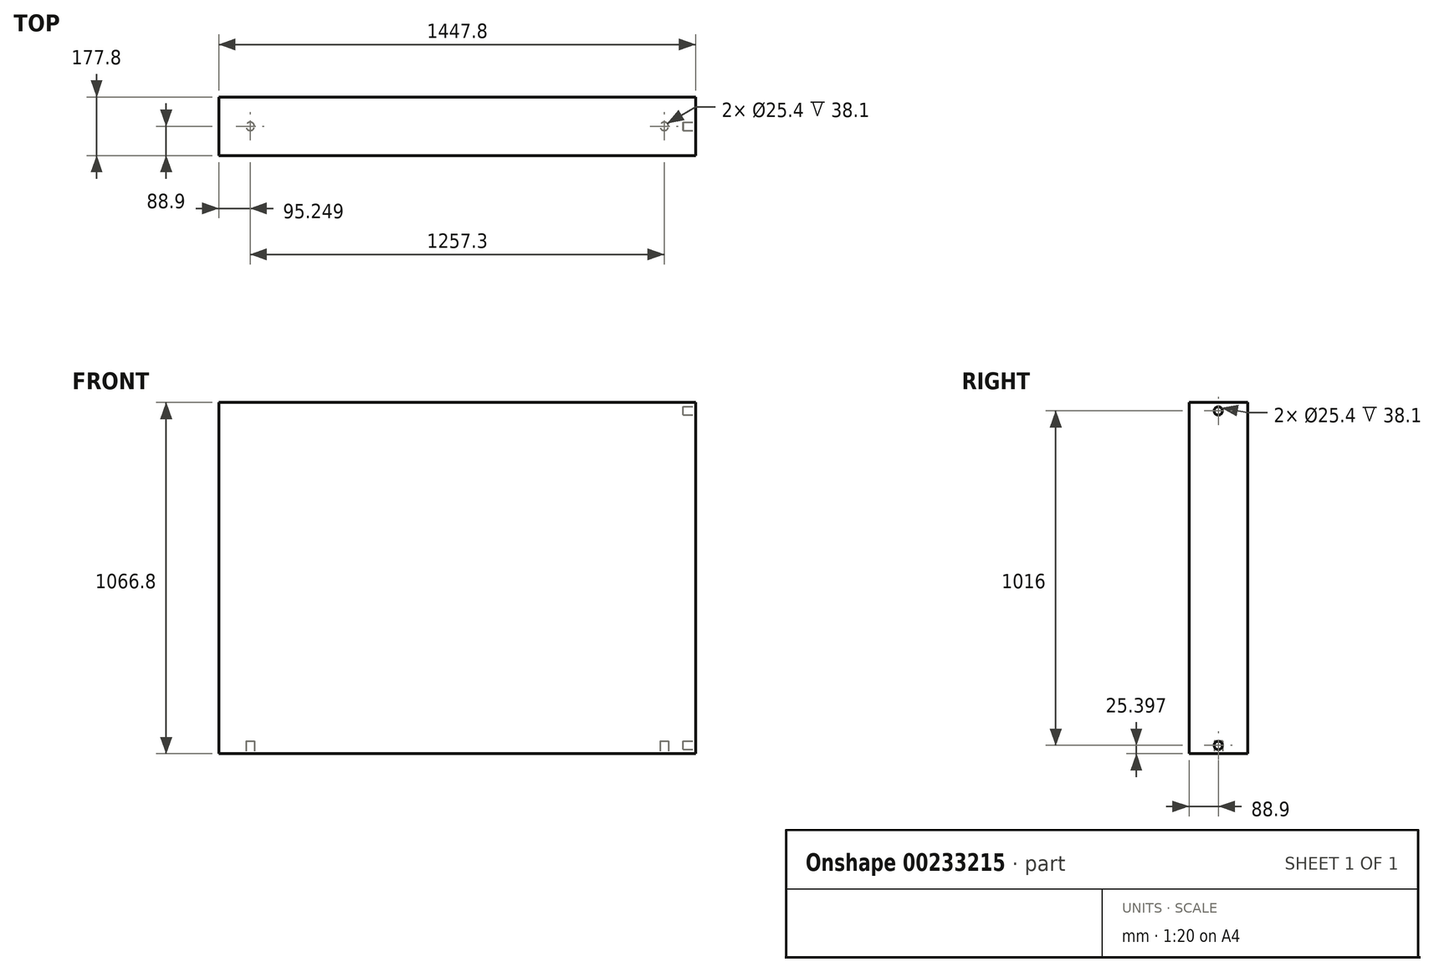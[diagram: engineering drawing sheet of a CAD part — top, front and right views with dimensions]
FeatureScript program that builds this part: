
annotation { "Feature Type Name" : "Feature", "Feature Type Description" : "" }
export const myFeature = defineFeature(function(context is Context, id is Id, definition is map)
    precondition{}
    {
        {
            var Q0;
            Q0=qCreatedBy(makeId("Front.planeOp"),FACE);
            var sketch = newSketch(context, id + "F0", { "sketchPlane" : qUnion([Q0])});
            skLineSegment(sketch, "E0.bottom", {"start": v(-749.86, 115.38) * mm, "end": v(697.94, 115.38) * mm});
            skLineSegment(sketch, "E0.top", {"start": v(-749.86, -951.42) * mm, "end": v(697.94, -951.42) * mm});
            skLineSegment(sketch, "E0.left", {"start": v(-749.86, 115.38) * mm, "end": v(-749.86, -951.42) * mm});
            skLineSegment(sketch, "E0.right", {"start": v(697.94, 115.38) * mm, "end": v(697.94, -951.42) * mm});
            skSolve(sketch);
        }
        {
            var Q0;
            Q0 = qSketchRegion(id + "F0", true);
            extrude(context, id + "F1", {"entities" : qUnion([Q0]), "depth" : 177.8 * mm});
        }
        {
            var Q0;
            Q0=makeQuery(id+"F1.opExtrude","SWEPT_FACE",FACE,{"disambiguationData":[OSD([sQuery(id+"F0.wireOp",EDGE,"E0.top")])]});
            var sketch = newSketch(context, id + "F2", { "sketchPlane" : qUnion([Q0])});
            skCircle(sketch, "E1", {"center": v(-654.61, 88.9) * mm, "radius": 12.7 * mm});
            skLineSegment(sketch, "E2", {"start": v(-657.5, 177.8) * mm, "end": v(-749.86, 177.8) * mm});
            skLineSegment(sketch, "E3", {"start": v(-749.86, 177.8) * mm, "end": v(-749.86, 0) * mm});
            skLineSegment(sketch, "E4", {"start": v(-749.86, 0) * mm, "end": v(-659.45, 0) * mm});
            skCircle(sketch, "E5", {"center": v(602.69, 88.9) * mm, "radius": 12.7 * mm});
            skLineSegment(sketch, "E6", {"start": v(591.78, 177.8) * mm, "end": v(697.94, 177.8) * mm});
            skLineSegment(sketch, "E7", {"start": v(697.94, 177.8) * mm, "end": v(697.94, 0) * mm});
            skSolve(sketch);
        }
        {
            var Q0;
            Q0 = qSketchRegion(id + "F2", true);
            extrude(context, id + "F3", {"entities" : qUnion([Q0]), "operationType" : NewBodyOperationType.REMOVE, "oppositeDirection" : true, "depth" : 38.1 * mm});
        }
        {
            var Q0;
            Q0=makeQuery(id+"F1.opExtrude","SWEPT_FACE",FACE,{"disambiguationData":[OSD([sQuery(id+"F0.wireOp",EDGE,"E0.right")])]});
            var sketch = newSketch(context, id + "F4", { "sketchPlane" : qUnion([Q0])});
            skCircle(sketch, "E8", {"center": v(-88.9, 89.98) * mm, "radius": 12.7 * mm});
            skCircle(sketch, "E9", {"center": v(-88.9, -926.02) * mm, "radius": 12.7 * mm});
            skSolve(sketch);
        }
        {
            var Q0;
            Q0 = qSketchRegion(id + "F4", true);
            extrude(context, id + "F5", {"entities" : qUnion([Q0]), "operationType" : NewBodyOperationType.REMOVE, "oppositeDirection" : true, "depth" : 38.1 * mm});
        }
    });
